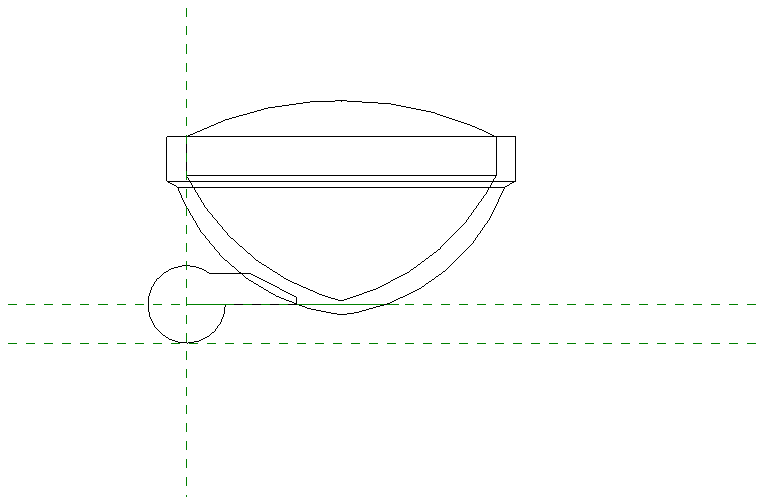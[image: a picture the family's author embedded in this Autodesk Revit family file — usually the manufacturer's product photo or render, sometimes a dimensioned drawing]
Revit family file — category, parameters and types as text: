
# Revit family: OCR- Double
name_source: partatom
category: Lighting Fixtures
revit_build: Autodesk Revit MEP 2012 (Build: 20110916_2132(x64)
units: mm (PartAtom-declared; Revit-internal decimal feet)

## types (3) — shared parameters
Apparent Load = 5 VA
Default Elevation = 48.000"
Description = Outdoor UL Wet Location Listed die cast aluminum lamp head and 
mounting plate assembly complete with MR 16 lamp.
Load Classification = Lighting
Manufacturer = Dual-lite
Manufacturer Fax = 866-898-0131
Model = OCR-Double
Product Documentation Link = http://cdn.dual-lite.com
Product Page URL = http://www.dual-lite.com
Total Input Wattage = 5 W
URL = http://www.dual-lite.com
Voltage = 120 V

## per-type parameters (varying)
| type | Lamp | Material Finish | Photometric Web |
| OCR Double- White | Halogen MR16, LED | Hubbell-Aluminum- White | Web OCR : OCR Series with 3W LED Lamp |
| OCR Double- Black | Halogen MR16 | Hubbell-Aluminum- Black | Web OCR : OCR Series with 3W LED Lamp |
| OCR Double- Dark Bronze | Halogen MR16 | Hubbell-Aluminum-Dark Bronze | Web OCR : OCR Series with 12V, 5W Lamp |

## geometry (parser evidence)
native form markers: Blend x18, Sweep x3
no freeform markers — native parametric forms only
